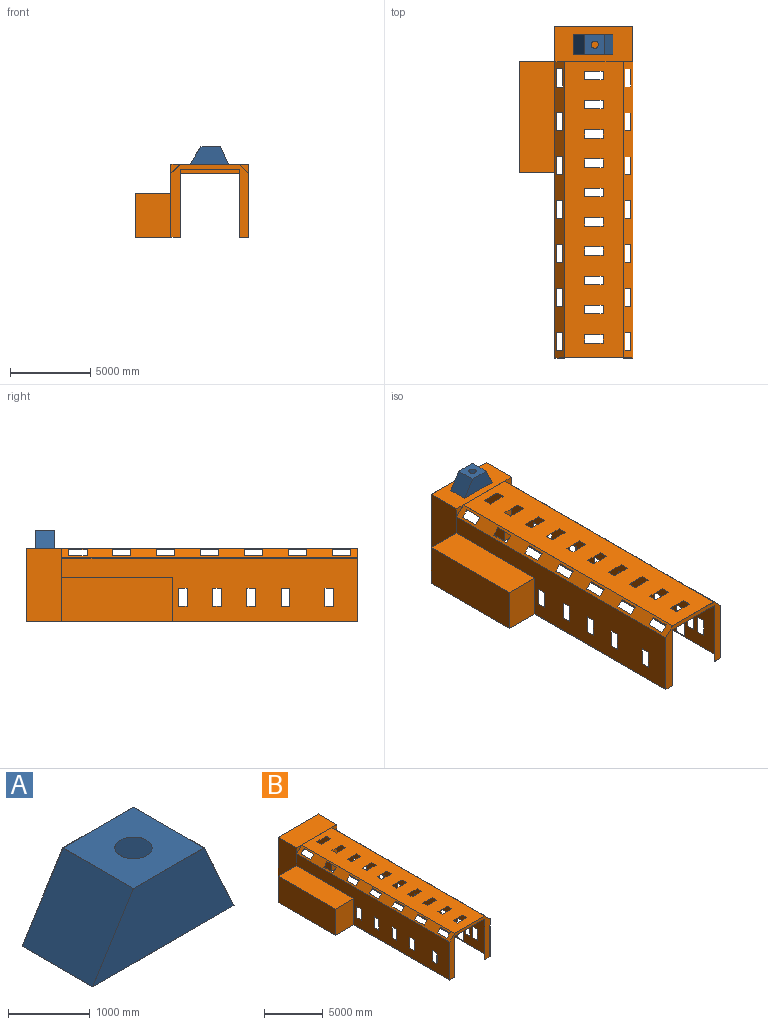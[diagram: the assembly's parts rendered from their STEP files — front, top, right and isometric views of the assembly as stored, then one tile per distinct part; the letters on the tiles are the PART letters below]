
ASSEMBLY  parts=2 mates=1
PART A: 12 faces, bbox 2438.4x1219.2x1117.6 mm
  f0: plane 2438.4x1219.2mm, normal (0,0,-1), area 19427.5mm2, adj f1,f2,f4,f5,f6,f7,f9,f10
  f1: plane 1219.2x1117.6mm, normal (-0.85,0,0.53), area 1610357.3mm2, adj f0,f3,f4,f5
  f2: plane 1219.2x1117.6mm, normal (0.91,0,0.42), area 1500407.8mm2, adj f0,f3,f4,f5
  f3: plane 1219.2x1219.2mm, normal (0,0,1), area 1322275.4mm2, adj f1,f2,f4,f5,f11
  f4: plane 2438.4x1117.6mm, normal (0,-1,0), area 2043866.9mm2, adj f0,f1,f2,f3
  f5: plane 2438.4x1117.6mm, normal (0,1,0), area 2043866.9mm2, adj f0,f1,f2,f3
  f6: plane 1214.12x1115.06mm, normal (0.85,0,-0.53), area 1600002.8mm2, adj f0,f8,f9,f10
  f7: plane 1214.12x1115.06mm, normal (-0.91,0,-0.42), area 1490760.3mm2, adj f0,f8,f9,f10
  f8: plane 1216.17x1214.12mm, normal (0,0,-1), area 1312405.6mm2, adj f6,f7,f9,f10,f11
  f9: plane 2432.6x1115.06mm, normal (0,1,0), area 2034300.6mm2, adj f0,f6,f7,f8
  f10: plane 2432.6x1115.06mm, normal (0,-1,0), area 2034300.6mm2, adj f0,f6,f7,f8
  f11: cylinder r=228.6mm len=457.2mm, axis (0,0,1), area 3648.3mm2, adj f3,f8
PART B: 238 faces, bbox 7112x20726.4x4572 mm
  f0: plane 20726.4x4572mm, normal (1,0,0), area 75231720.5mm2, adj f5,f7,f10,f12,f14,f24,f25,f26
  f1: plane 18485.1x3961.14mm, normal (-1,0,0), area 64967216mm2, adj f5,f11,f15,f16,f24,f25,f26,f123
  f2: plane 18485.1x3961.14mm, normal (1,0,0), area 67612372mm2, adj f9,f15,f16,f17,f124,f125,f126,f127
  f3: plane 6916.42x2740.66mm, normal (-1,0,0), area 16377186.6mm2, adj f17,f217,f218,f219,f222,f223,f224,f225
  f4: plane 20726.4x4572mm, normal (-1,0,0), area 61453425.5mm2, adj f7,f8,f12,f14,f17,f124,f125,f126
  f5: plane 20726.4x609.6mm, normal (0,0,-1), area 1422636.6mm2, adj f0,f1,f7,f14,f15,f16,f19,f22
  f6: plane 3657.6x304.8mm, normal (0,-1,0), area 1114836.5mm2, adj f18,f19,f20,f194
  f7: plane 4876.8x4572mm, normal (0,1,0), area 7803855.4mm2, adj f0,f4,f5,f12,f17,f19,f20,f194
  f8: plane 18491.2x609.6mm, normal (-0.71,0,0.71), area 11673614.9mm2, adj f4,f12,f14,f95,f96,f97,f98,f99
  f9: plane 18485.1x607.81mm, normal (0.71,0,-0.71), area 11621683.8mm2, adj f2,f13,f15,f16,f95,f96,f97,f98
  f10: plane 18491.2x609.6mm, normal (0.71,0,0.71), area 11673614.9mm2, adj f0,f12,f14,f67,f68,f69,f70,f71
  f11: plane 18485.1x607.81mm, normal (-0.71,0,-0.71), area 11621683.8mm2, adj f1,f13,f15,f16,f67,f68,f69,f70
  f12: plane 20726.4x4876.8mm, normal (0,0,1), area 72437274.5mm2, adj f0,f4,f7,f8,f10,f14,f27,f28
  f13: plane 18485.1x3655.08mm, normal (0,0,-1), area 61467678.7mm2, adj f9,f11,f15,f16,f27,f28,f29,f30
  f14: plane 4876.8x4572mm, normal (0,-1,0), area 6317406.7mm2, adj f0,f4,f5,f8,f10,f12,f17,f21
  f15: plane 4870.7x4568.95mm, normal (0,1,0), area 6276863.6mm2, adj f1,f2,f5,f9,f11,f13,f17,f21
  f16: plane 4870.7x4568.95mm, normal (0,-1,0), area 6276863.6mm2, adj f1,f2,f5,f9,f11,f13,f17,f18
  f17: plane 20726.4x2844.8mm, normal (0,0,-1), area 98050.9mm2, adj f2,f3,f4,f7,f14,f15,f16,f20
  f18: plane 3657.6x3.05mm, normal (0,0,-1), area 11148.4mm2, adj f6,f16,f19,f20
  f19: plane 4267.2x2238.25mm, normal (-1,0,0), area 8869762.9mm2, adj f5,f6,f7,f16,f18,f194
  f20: plane 4267.2x2238.25mm, normal (1,0,0), area 8869762.9mm2, adj f6,f7,f16,f17,f18,f194
  f21: plane 4267.2x3.05mm, normal (1,0,0), area 13006.4mm2, adj f14,f15,f17,f23
  f22: plane 4267.2x3.05mm, normal (-1,0,0), area 13006.4mm2, adj f5,f14,f15,f23
  f23: plane 3657.6x3.05mm, normal (0,0,-1), area 11148.4mm2, adj f14,f15,f21,f22
  f24: plane 2035.05x3.05mm, normal (0,1,0), area 6198.2mm2, adj f0,f1,f26,f123
  f25: plane 2035.05x3.05mm, normal (0,-1,0), area 6198.2mm2, adj f0,f1,f26,f123
  f26: plane 762x3.05mm, normal (0,0,-1), area 2322.6mm2, adj f0,f1,f24,f25
  f27: plane 533.4x3.05mm, normal (1,0,0), area 1625.8mm2, adj f12,f13,f28,f30
  f28: plane 1143x3.05mm, normal (0,1,0), area 3483.9mm2, adj f12,f13,f27,f29
  f29: plane 533.4x3.05mm, normal (-1,0,0), area 1625.8mm2, adj f12,f13,f28,f30
  f30: plane 1143x3.05mm, normal (0,-1,0), area 3483.9mm2, adj f12,f13,f27,f29
  f31: plane 533.4x3.05mm, normal (1,0,0), area 1625.8mm2, adj f12,f13,f32,f34
  f32: plane 1143x3.05mm, normal (0,1,0), area 3483.9mm2, adj f12,f13,f31,f33
  f33: plane 533.4x3.05mm, normal (-1,0,0), area 1625.8mm2, adj f12,f13,f32,f34
  f34: plane 1143x3.05mm, normal (0,-1,0), area 3483.9mm2, adj f12,f13,f31,f33
  f35: plane 533.4x3.05mm, normal (1,0,0), area 1625.8mm2, adj f12,f13,f36,f38
  f36: plane 1143x3.05mm, normal (0,1,0), area 3483.9mm2, adj f12,f13,f35,f37
  f37: plane 533.4x3.05mm, normal (-1,0,0), area 1625.8mm2, adj f12,f13,f36,f38
  f38: plane 1143x3.05mm, normal (0,-1,0), area 3483.9mm2, adj f12,f13,f35,f37
  f39: plane 533.4x3.05mm, normal (1,0,0), area 1625.8mm2, adj f12,f13,f40,f42
  f40: plane 1143x3.05mm, normal (0,1,0), area 3483.9mm2, adj f12,f13,f39,f41
  f41: plane 533.4x3.05mm, normal (-1,0,0), area 1625.8mm2, adj f12,f13,f40,f42
  f42: plane 1143x3.05mm, normal (0,-1,0), area 3483.9mm2, adj f12,f13,f39,f41
  f43: plane 533.4x3.05mm, normal (1,0,0), area 1625.8mm2, adj f12,f13,f44,f46
  f44: plane 1143x3.05mm, normal (0,1,0), area 3483.9mm2, adj f12,f13,f43,f45
  f45: plane 533.4x3.05mm, normal (-1,0,0), area 1625.8mm2, adj f12,f13,f44,f46
  f46: plane 1143x3.05mm, normal (0,-1,0), area 3483.9mm2, adj f12,f13,f43,f45
  f47: plane 533.4x3.05mm, normal (1,0,0), area 1625.8mm2, adj f12,f13,f48,f50
  f48: plane 1143x3.05mm, normal (0,1,0), area 3483.9mm2, adj f12,f13,f47,f49
  f49: plane 533.4x3.05mm, normal (-1,0,0), area 1625.8mm2, adj f12,f13,f48,f50
  f50: plane 1143x3.05mm, normal (0,-1,0), area 3483.9mm2, adj f12,f13,f47,f49
  f51: plane 533.4x3.05mm, normal (1,0,0), area 1625.8mm2, adj f12,f13,f52,f54
  f52: plane 1143x3.05mm, normal (0,1,0), area 3483.9mm2, adj f12,f13,f51,f53
  f53: plane 533.4x3.05mm, normal (-1,0,0), area 1625.8mm2, adj f12,f13,f52,f54
  f54: plane 1143x3.05mm, normal (0,-1,0), area 3483.9mm2, adj f12,f13,f51,f53
  f55: plane 533.4x3.05mm, normal (1,0,0), area 1625.8mm2, adj f12,f13,f56,f58
  f56: plane 1143x3.05mm, normal (0,1,0), area 3483.9mm2, adj f12,f13,f55,f57
  f57: plane 533.4x3.05mm, normal (-1,0,0), area 1625.8mm2, adj f12,f13,f56,f58
  f58: plane 1143x3.05mm, normal (0,-1,0), area 3483.9mm2, adj f12,f13,f55,f57
  f59: plane 533.4x3.05mm, normal (1,0,0), area 1625.8mm2, adj f12,f13,f60,f62
  f60: plane 1143x3.05mm, normal (0,1,0), area 3483.9mm2, adj f12,f13,f59,f61
  f61: plane 533.4x3.05mm, normal (-1,0,0), area 1625.8mm2, adj f12,f13,f60,f62
  f62: plane 1143x3.05mm, normal (0,-1,0), area 3483.9mm2, adj f12,f13,f59,f61
  f63: plane 533.4x3.05mm, normal (1,0,0), area 1625.8mm2, adj f12,f13,f64,f66
  f64: plane 1143x3.05mm, normal (0,1,0), area 3483.9mm2, adj f12,f13,f63,f65
  f65: plane 533.4x3.05mm, normal (-1,0,0), area 1625.8mm2, adj f12,f13,f64,f66
  f66: plane 1143x3.05mm, normal (0,-1,0), area 3483.9mm2, adj f12,f13,f63,f65
  f67: plane 1143x2.16mm, normal (0.71,0,-0.71), area 3483.9mm2, adj f10,f11,f68,f70
  f68: plane 379.33x379.33mm, normal (0,1,0), area 1625.8mm2, adj f10,f11,f67,f69
  f69: plane 1143x2.16mm, normal (-0.71,0,0.71), area 3483.9mm2, adj f10,f11,f68,f70
  f70: plane 379.33x379.33mm, normal (0,-1,0), area 1625.8mm2, adj f10,f11,f67,f69
  f71: plane 1143x2.16mm, normal (0.71,0,-0.71), area 3483.9mm2, adj f10,f11,f72,f74
  f72: plane 379.33x379.33mm, normal (0,1,0), area 1625.8mm2, adj f10,f11,f71,f73
  f73: plane 1143x2.16mm, normal (-0.71,0,0.71), area 3483.9mm2, adj f10,f11,f72,f74
  f74: plane 379.33x379.33mm, normal (0,-1,0), area 1625.8mm2, adj f10,f11,f71,f73
  f75: plane 1143x2.16mm, normal (0.71,0,-0.71), area 3483.9mm2, adj f10,f11,f76,f78
  f76: plane 379.33x379.33mm, normal (0,1,0), area 1625.8mm2, adj f10,f11,f75,f77
  f77: plane 1143x2.16mm, normal (-0.71,0,0.71), area 3483.9mm2, adj f10,f11,f76,f78
  f78: plane 379.33x379.33mm, normal (0,-1,0), area 1625.8mm2, adj f10,f11,f75,f77
  f79: plane 1143x2.16mm, normal (0.71,0,-0.71), area 3483.9mm2, adj f10,f11,f80,f82
  f80: plane 379.33x379.33mm, normal (0,1,0), area 1625.8mm2, adj f10,f11,f79,f81
  f81: plane 1143x2.16mm, normal (-0.71,0,0.71), area 3483.9mm2, adj f10,f11,f80,f82
  f82: plane 379.33x379.33mm, normal (0,-1,0), area 1625.8mm2, adj f10,f11,f79,f81
  f83: plane 1143x2.16mm, normal (0.71,0,-0.71), area 3483.9mm2, adj f10,f11,f84,f86
  f84: plane 379.33x379.33mm, normal (0,1,0), area 1625.8mm2, adj f10,f11,f83,f85
  f85: plane 1143x2.16mm, normal (-0.71,0,0.71), area 3483.9mm2, adj f10,f11,f84,f86
  f86: plane 379.33x379.33mm, normal (0,-1,0), area 1625.8mm2, adj f10,f11,f83,f85
  f87: plane 1143x2.16mm, normal (0.71,0,-0.71), area 3483.9mm2, adj f10,f11,f88,f90
  f88: plane 379.33x379.33mm, normal (0,1,0), area 1625.8mm2, adj f10,f11,f87,f89
  f89: plane 1143x2.16mm, normal (-0.71,0,0.71), area 3483.9mm2, adj f10,f11,f88,f90
  f90: plane 379.33x379.33mm, normal (0,-1,0), area 1625.8mm2, adj f10,f11,f87,f89
  f91: plane 1143x2.16mm, normal (0.71,0,-0.71), area 3483.9mm2, adj f10,f11,f92,f94
  f92: plane 379.33x379.33mm, normal (0,1,0), area 1625.8mm2, adj f10,f11,f91,f93
  f93: plane 1143x2.16mm, normal (-0.71,0,0.71), area 3483.9mm2, adj f10,f11,f92,f94
  f94: plane 379.33x379.33mm, normal (0,-1,0), area 1625.8mm2, adj f10,f11,f91,f93
  f95: plane 379.33x379.33mm, normal (0,1,0), area 1625.8mm2, adj f8,f9,f96,f98
  f96: plane 1143x2.16mm, normal (-0.71,0,-0.71), area 3483.9mm2, adj f8,f9,f95,f97
  f97: plane 379.33x379.33mm, normal (0,-1,0), area 1625.8mm2, adj f8,f9,f96,f98
  f98: plane 1143x2.16mm, normal (0.71,0,0.71), area 3483.9mm2, adj f8,f9,f95,f97
  f99: plane 379.33x379.33mm, normal (0,1,0), area 1625.8mm2, adj f8,f9,f100,f102
  f100: plane 1143x2.16mm, normal (-0.71,0,-0.71), area 3483.9mm2, adj f8,f9,f99,f101
  f101: plane 379.33x379.33mm, normal (0,-1,0), area 1625.8mm2, adj f8,f9,f100,f102
  f102: plane 1143x2.16mm, normal (0.71,0,0.71), area 3483.9mm2, adj f8,f9,f99,f101
  f103: plane 379.33x379.33mm, normal (0,1,0), area 1625.8mm2, adj f8,f9,f104,f106
  f104: plane 1143x2.16mm, normal (-0.71,0,-0.71), area 3483.9mm2, adj f8,f9,f103,f105
  f105: plane 379.33x379.33mm, normal (0,-1,0), area 1625.8mm2, adj f8,f9,f104,f106
  f106: plane 1143x2.16mm, normal (0.71,0,0.71), area 3483.9mm2, adj f8,f9,f103,f105
  f107: plane 379.33x379.33mm, normal (0,1,0), area 1625.8mm2, adj f8,f9,f108,f110
  f108: plane 1143x2.16mm, normal (-0.71,0,-0.71), area 3483.9mm2, adj f8,f9,f107,f109
  f109: plane 379.33x379.33mm, normal (0,-1,0), area 1625.8mm2, adj f8,f9,f108,f110
  f110: plane 1143x2.16mm, normal (0.71,0,0.71), area 3483.9mm2, adj f8,f9,f107,f109
  f111: plane 379.33x379.33mm, normal (0,1,0), area 1625.8mm2, adj f8,f9,f112,f114
  f112: plane 1143x2.16mm, normal (-0.71,0,-0.71), area 3483.9mm2, adj f8,f9,f111,f113
  f113: plane 379.33x379.33mm, normal (0,-1,0), area 1625.8mm2, adj f8,f9,f112,f114
  f114: plane 1143x2.16mm, normal (0.71,0,0.71), area 3483.9mm2, adj f8,f9,f111,f113
  f115: plane 379.33x379.33mm, normal (0,1,0), area 1625.8mm2, adj f8,f9,f116,f118
  f116: plane 1143x2.16mm, normal (-0.71,0,-0.71), area 3483.9mm2, adj f8,f9,f115,f117
  f117: plane 379.33x379.33mm, normal (0,-1,0), area 1625.8mm2, adj f8,f9,f116,f118
  f118: plane 1143x2.16mm, normal (0.71,0,0.71), area 3483.9mm2, adj f8,f9,f115,f117
  f119: plane 379.33x379.33mm, normal (0,1,0), area 1625.8mm2, adj f8,f9,f120,f122
  f120: plane 1143x2.16mm, normal (-0.71,0,-0.71), area 3483.9mm2, adj f8,f9,f119,f121
  f121: plane 379.33x379.33mm, normal (0,-1,0), area 1625.8mm2, adj f8,f9,f120,f122
  f122: plane 1143x2.16mm, normal (0.71,0,0.71), area 3483.9mm2, adj f8,f9,f119,f121
  f123: plane 762x3.05mm, normal (0.71,0,0.71), area 3284.6mm2, adj f0,f1,f24,f25
  f124: plane 1143x3.05mm, normal (0,-1,0), area 3483.9mm2, adj f2,f4,f125,f127
  f125: plane 533.4x3.05mm, normal (0,0,1), area 1625.8mm2, adj f2,f4,f124,f126
  f126: plane 1143x3.05mm, normal (0,1,0), area 3483.9mm2, adj f2,f4,f125,f127
  f127: plane 533.4x3.05mm, normal (0,0,-1), area 1625.8mm2, adj f2,f4,f124,f126
  f128: plane 533.4x3.05mm, normal (0,0,-1), area 1625.8mm2, adj f0,f1,f129,f131
  f129: plane 1143x3.05mm, normal (0,1,0), area 3483.9mm2, adj f0,f1,f128,f130
  f130: plane 533.4x3.05mm, normal (0,0,1), area 1625.8mm2, adj f0,f1,f129,f131
  f131: plane 1143x3.05mm, normal (0,-1,0), area 3483.9mm2, adj f0,f1,f128,f130
  f132: plane 533.4x3.05mm, normal (0,0,-1), area 1625.8mm2, adj f0,f1,f133,f135
  f133: plane 1143x3.05mm, normal (0,1,0), area 3483.9mm2, adj f0,f1,f132,f134
  f134: plane 533.4x3.05mm, normal (0,0,1), area 1625.8mm2, adj f0,f1,f133,f135
  f135: plane 1143x3.05mm, normal (0,-1,0), area 3483.9mm2, adj f0,f1,f132,f134
  f136: plane 1143x3.05mm, normal (0,-1,0), area 3483.9mm2, adj f2,f137,f139,f196
  f137: plane 533.4x3.05mm, normal (0,0,1), area 1625.8mm2, adj f2,f136,f138,f196
  f138: plane 1143x3.05mm, normal (0,1,0), area 3483.9mm2, adj f2,f137,f139,f196
  f139: plane 533.4x3.05mm, normal (0,0,-1), area 1625.8mm2, adj f2,f136,f138,f196
  f140: plane 1143x3.05mm, normal (0,-1,0), area 3483.9mm2, adj f2,f4,f141,f143
  f141: plane 533.4x3.05mm, normal (0,0,1), area 1625.8mm2, adj f2,f4,f140,f142
  f142: plane 1143x3.05mm, normal (0,1,0), area 3483.9mm2, adj f2,f4,f141,f143
  f143: plane 533.4x3.05mm, normal (0,0,-1), area 1625.8mm2, adj f2,f4,f140,f142
  f144: plane 1143x3.05mm, normal (0,-1,0), area 3483.9mm2, adj f2,f4,f145,f147
  f145: plane 533.4x3.05mm, normal (0,0,1), area 1625.8mm2, adj f2,f4,f144,f146
  f146: plane 1143x3.05mm, normal (0,1,0), area 3483.9mm2, adj f2,f4,f145,f147
  f147: plane 533.4x3.05mm, normal (0,0,-1), area 1625.8mm2, adj f2,f4,f144,f146
  f148: plane 1143x3.05mm, normal (0,-1,0), area 3483.9mm2, adj f2,f4,f149,f151
  f149: plane 533.4x3.05mm, normal (0,0,1), area 1625.8mm2, adj f2,f4,f148,f150
  f150: plane 1143x3.05mm, normal (0,1,0), area 3483.9mm2, adj f2,f4,f149,f151
  f151: plane 533.4x3.05mm, normal (0,0,-1), area 1625.8mm2, adj f2,f4,f148,f150
  f152: plane 1143x3.05mm, normal (0,-1,0), area 3483.9mm2, adj f2,f153,f155,f195
  f153: plane 533.4x3.05mm, normal (0,0,1), area 1625.8mm2, adj f2,f152,f154,f195
  f154: plane 1143x3.05mm, normal (0,1,0), area 3483.9mm2, adj f2,f153,f155,f195
  f155: plane 533.4x3.05mm, normal (0,0,-1), area 1625.8mm2, adj f2,f152,f154,f195
  f156: plane 1143x3.05mm, normal (0,-1,0), area 3483.9mm2, adj f2,f4,f157,f159
  f157: plane 533.4x3.05mm, normal (0,0,1), area 1625.8mm2, adj f2,f4,f156,f158
  f158: plane 1143x3.05mm, normal (0,1,0), area 3483.9mm2, adj f2,f4,f157,f159
  f159: plane 533.4x3.05mm, normal (0,0,-1), area 1625.8mm2, adj f2,f4,f156,f158
  f160: plane 533.4x3.05mm, normal (0,0,-1), area 1625.8mm2, adj f0,f1,f161,f163
  f161: plane 1143x3.05mm, normal (0,1,0), area 3483.9mm2, adj f0,f1,f160,f162
  f162: plane 533.4x3.05mm, normal (0,0,1), area 1625.8mm2, adj f0,f1,f161,f163
  f163: plane 1143x3.05mm, normal (0,-1,0), area 3483.9mm2, adj f0,f1,f160,f162
  f164: plane 533.4x3.05mm, normal (0,0,-1), area 1625.8mm2, adj f0,f1,f165,f167
  f165: plane 1143x3.05mm, normal (0,1,0), area 3483.9mm2, adj f0,f1,f164,f166
  f166: plane 533.4x3.05mm, normal (0,0,1), area 1625.8mm2, adj f0,f1,f165,f167
  f167: plane 1143x3.05mm, normal (0,-1,0), area 3483.9mm2, adj f0,f1,f164,f166
  f168: plane 533.4x3.05mm, normal (0,0,-1), area 1625.8mm2, adj f0,f1,f169,f171
  f169: plane 1143x3.05mm, normal (0,1,0), area 3483.9mm2, adj f0,f1,f168,f170
  f170: plane 533.4x3.05mm, normal (0,0,1), area 1625.8mm2, adj f0,f1,f169,f171
  f171: plane 1143x3.05mm, normal (0,-1,0), area 3483.9mm2, adj f0,f1,f168,f170
  f172: plane 533.4x3.05mm, normal (0,0,-1), area 1625.8mm2, adj f0,f1,f173,f175
  f173: plane 1143x3.05mm, normal (0,1,0), area 3483.9mm2, adj f0,f1,f172,f174
  f174: plane 533.4x3.05mm, normal (0,0,1), area 1625.8mm2, adj f0,f1,f173,f175
  f175: plane 1143x3.05mm, normal (0,-1,0), area 3483.9mm2, adj f0,f1,f172,f174
  f176: plane 533.4x3.05mm, normal (0,0,-1), area 1625.8mm2, adj f0,f1,f177,f179
  f177: plane 1143x3.05mm, normal (0,1,0), area 3483.9mm2, adj f0,f1,f176,f178
  f178: plane 533.4x3.05mm, normal (0,0,1), area 1625.8mm2, adj f0,f1,f177,f179
  f179: plane 1143x3.05mm, normal (0,-1,0), area 3483.9mm2, adj f0,f1,f176,f178
  f180: plane 533.4x3.05mm, normal (0,0,-1), area 1625.8mm2, adj f0,f1,f181,f183
  f181: plane 1143x3.05mm, normal (0,1,0), area 3483.9mm2, adj f0,f1,f180,f182
  f182: plane 533.4x3.05mm, normal (0,0,1), area 1625.8mm2, adj f0,f1,f181,f183
  f183: plane 1143x3.05mm, normal (0,-1,0), area 3483.9mm2, adj f0,f1,f180,f182
  f184: plane 533.4x3.05mm, normal (0,0,-1), area 1625.8mm2, adj f0,f1,f185,f187
  f185: plane 1143x3.05mm, normal (0,1,0), area 3483.9mm2, adj f0,f1,f184,f186
  f186: plane 533.4x3.05mm, normal (0,0,1), area 1625.8mm2, adj f0,f1,f185,f187
  f187: plane 1143x3.05mm, normal (0,-1,0), area 3483.9mm2, adj f0,f1,f184,f186
  f188: plane 533.4x3.05mm, normal (0,0,-1), area 1625.8mm2, adj f0,f1,f189,f191
  f189: plane 1143x3.05mm, normal (0,1,0), area 3483.9mm2, adj f0,f1,f188,f190
  f190: plane 533.4x3.05mm, normal (0,0,1), area 1625.8mm2, adj f0,f1,f189,f191
  f191: plane 1143x3.05mm, normal (0,-1,0), area 3483.9mm2, adj f0,f1,f188,f190
  f192: plane 609.6x609.6mm, normal (0,-1,0), area 185806.1mm2, adj f4,f8,f12
  f193: plane 609.6x609.6mm, normal (0,-1,0), area 185806.1mm2, adj f0,f10,f12
  f194: plane 3657.6x2235.2mm, normal (0,0,-1), area 8175467.5mm2, adj f6,f7,f19,f20
  f195: plane 1143x533.4mm, normal (1,0,0), area 609676.2mm2, adj f152,f153,f154,f155
  f196: plane 1143x533.4mm, normal (1,0,0), area 609676.2mm2, adj f136,f137,f138,f139
  f197: plane 2743.2x2235.2mm, normal (0,1,0), area 6131600.6mm2, adj f4,f17,f199,f200
  f198: plane 2743.2x2235.2mm, normal (0,-1,0), area 6131600.6mm2, adj f4,f17,f199,f200
  f199: plane 6921.5x2235.2mm, normal (0,0,1), area 15470936.8mm2, adj f4,f197,f198,f200
  f200: plane 6921.5x2743.2mm, normal (-1,0,0), area 18987058.8mm2, adj f17,f197,f198,f199
  f201: plane 4569.46x2233.17mm, normal (1,0,0), area 10202518.3mm2, adj f17,f204,f206,f208,f209,f213
  f202: plane 2233.17x604.52mm, normal (0,0,1), area 1349994.7mm2, adj f204,f205,f209,f211
  f203: plane 3662.68x304.8mm, normal (0,1,0), area 1116384.9mm2, adj f210,f211,f212,f215
  f204: plane 4871.72x4569.46mm, normal (0,-1,0), area 7737287.8mm2, adj f17,f201,f202,f205,f208,f211,f212,f215
  f205: plane 4566.92x2233.17mm, normal (-1,0,0), area 10196846.1mm2, adj f202,f204,f207,f208,f209,f214
  f206: plane 608.11x608.11mm, normal (0.71,0,-0.71), area 2621.3mm2, adj f201,f208,f209,f213
  f207: plane 608.11x608.11mm, normal (-0.71,0,-0.71), area 2621.3mm2, adj f205,f208,f209,f214
  f208: plane 4871.72x2233.17mm, normal (0,0,-1), area 10875662.2mm2, adj f201,f204,f205,f206,f207,f209,f213,f214
  f209: plane 4871.72x4569.46mm, normal (0,1,0), area 6251102.6mm2, adj f17,f201,f202,f205,f206,f207,f208,f210
  f210: plane 3662.68x3.05mm, normal (0,0,1), area 11163.8mm2, adj f203,f209,f211,f212
  f211: plane 4267.2x2233.17mm, normal (1,0,0), area 8849633.9mm2, adj f202,f203,f204,f209,f210,f215
  f212: plane 4269.74x2233.17mm, normal (-1,0,0), area 8855306.2mm2, adj f17,f203,f204,f209,f210,f215
  f213: plane 608.11x608.11mm, normal (0,1,0), area 184900.2mm2, adj f201,f206,f208
  f214: plane 608.11x608.11mm, normal (0,1,0), area 184900.2mm2, adj f205,f207,f208
  f215: plane 3662.68x2230.12mm, normal (0,0,1), area 8168215.9mm2, adj f203,f204,f211,f212
  f216: plane 6916.42x2740.66mm, normal (1,0,0), area 18955555.6mm2, adj f17,f217,f218,f219
  f217: plane 6916.42x2233.17mm, normal (0,0,-1), area 15445527.8mm2, adj f3,f216,f218,f219
  f218: plane 2740.66x2233.17mm, normal (0,1,0), area 6120354.2mm2, adj f3,f17,f216,f217
  f219: plane 2740.66x2233.17mm, normal (0,-1,0), area 6120354.2mm2, adj f3,f17,f216,f217
  f220: plane 1148.08x538.48mm, normal (-1,0,0), area 618218.1mm2, adj f226,f227,f228,f229
  f221: plane 1148.08x538.48mm, normal (-1,0,0), area 618218.1mm2, adj f222,f223,f224,f225
  f222: plane 538.48x3.05mm, normal (0,0,1), area 1641.3mm2, adj f3,f221,f223,f225
  f223: plane 1148.08x3.05mm, normal (0,-1,0), area 3499.3mm2, adj f3,f221,f222,f224
  f224: plane 538.48x3.05mm, normal (0,0,-1), area 1641.3mm2, adj f3,f221,f223,f225
  f225: plane 1148.08x3.05mm, normal (0,1,0), area 3499.3mm2, adj f3,f221,f222,f224
  f226: plane 538.48x3.05mm, normal (0,0,1), area 1641.3mm2, adj f3,f220,f227,f229
  f227: plane 1148.08x3.05mm, normal (0,-1,0), area 3499.3mm2, adj f3,f220,f226,f228
  f228: plane 538.48x3.05mm, normal (0,0,-1), area 1641.3mm2, adj f3,f220,f227,f229
  f229: plane 1148.08x3.05mm, normal (0,1,0), area 3499.3mm2, adj f3,f220,f226,f228
  f230: plane 660.4x2.54mm, normal (0,0,1), area 1677.4mm2, adj f2,f3,f231,f233
  f231: plane 2032x2.54mm, normal (0,-1,0), area 5161.3mm2, adj f2,f3,f230,f232
  f232: plane 660.4x2.54mm, normal (0,0,-1), area 1677.4mm2, adj f2,f3,f231,f233
  f233: plane 2032x2.54mm, normal (0,1,0), area 5161.3mm2, adj f2,f3,f230,f232
  f234: plane 1143x3.05mm, normal (0,1,0), area 3483.9mm2, adj f0,f1,f235,f237
  f235: plane 533.4x3.05mm, normal (0,0,1), area 1625.8mm2, adj f0,f1,f234,f236
  f236: plane 1143x3.05mm, normal (0,-1,0), area 3483.9mm2, adj f0,f1,f235,f237
  f237: plane 533.4x3.05mm, normal (0,0,-1), area 1625.8mm2, adj f0,f1,f234,f236
PLACE A t=(-5693.09,6745.01,-155.41)mm
PLACE B t=(-6870.35,5068.61,-4713.3)mm
MATE parallel A.f5 <-> B.f7  axis (0,1,0) through (-4431.95,6745.01,341.3)mm
